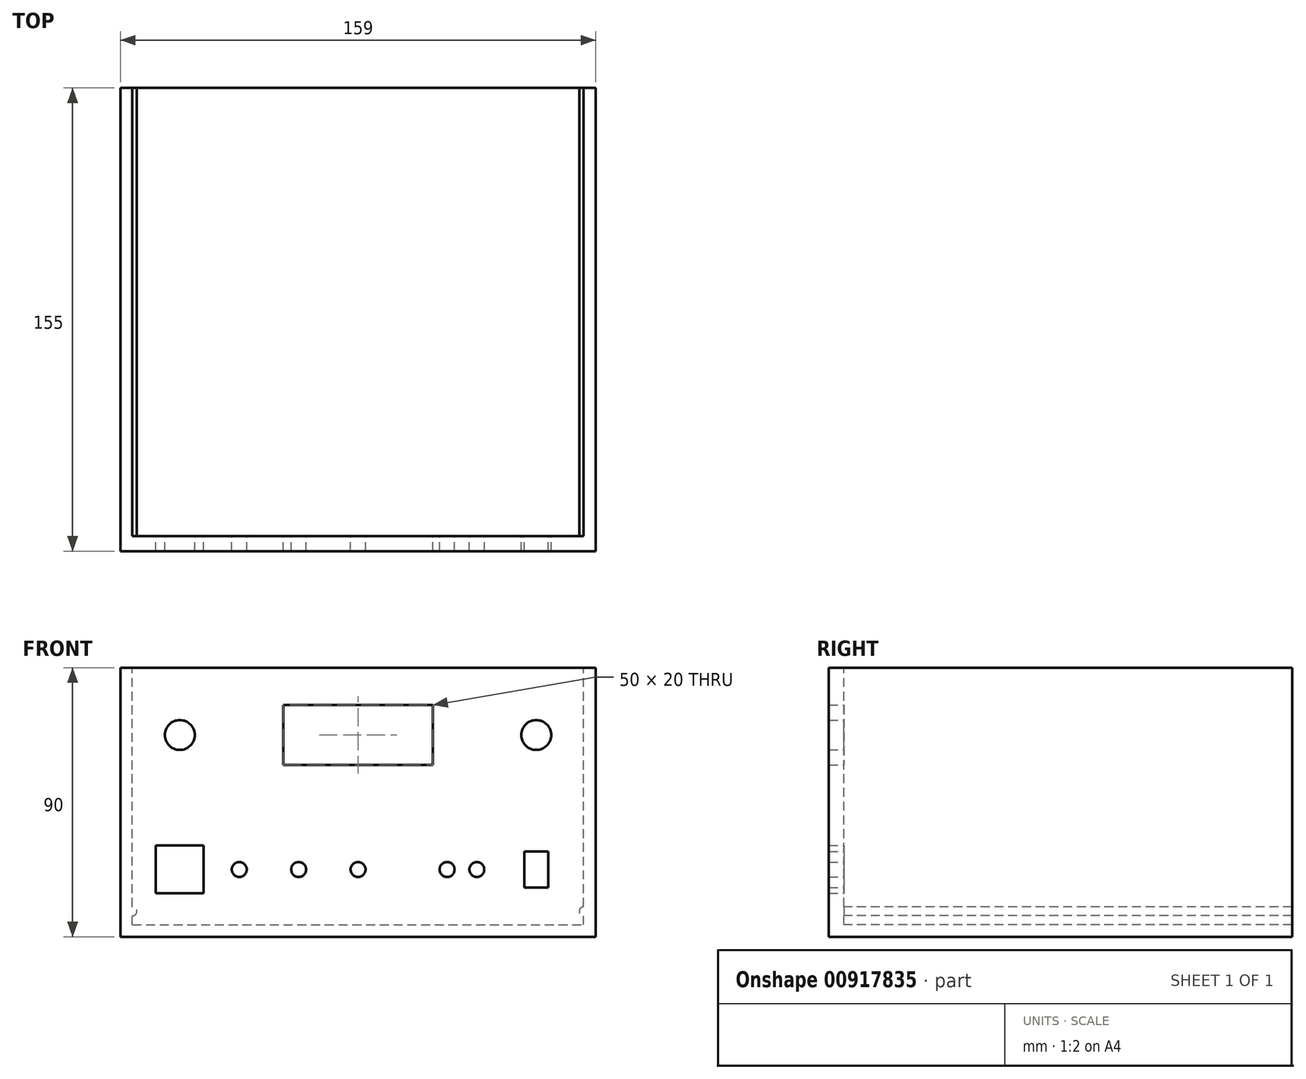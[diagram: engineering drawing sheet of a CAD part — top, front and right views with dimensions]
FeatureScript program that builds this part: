
annotation { "Feature Type Name" : "Feature", "Feature Type Description" : "" }
export const myFeature = defineFeature(function(context is Context, id is Id, definition is map)
    precondition{}
    {
        {
            var Q0;
            Q0=qCreatedBy(makeId("Front.planeOp"),FACE);
            var sketch = newSketch(context, id + "F0", { "sketchPlane" : qUnion([Q0])});
            skLineSegment(sketch, "E0.bottom", {"start": v(-79.5, 0) * mm, "end": v(79.5, 0) * mm});
            skLineSegment(sketch, "E0.top", {"start": v(-79.5, 90) * mm, "end": v(79.5, 90) * mm});
            skLineSegment(sketch, "E0.left", {"start": v(-79.5, 0) * mm, "end": v(-79.5, 90) * mm});
            skLineSegment(sketch, "E0.right", {"start": v(79.5, 0) * mm, "end": v(79.5, 90) * mm});
            skLineSegment(sketch, "E1", {"start": v(-79.5, 45) * mm, "end": v(0, 45) * mm, "construction": true});
            skLineSegment(sketch, "E2", {"start": v(0, 45) * mm, "end": v(-39.75, 45) * mm, "construction": true});
            skLineSegment(sketch, "E3", {"start": v(79.5, 45) * mm, "end": v(0, 45) * mm, "construction": true});
            skLineSegment(sketch, "E4", {"start": v(0, 45) * mm, "end": v(39.75, 45) * mm, "construction": true});
            skLineSegment(sketch, "E5", {"start": v(39.75, 45) * mm, "end": v(39.75, 90) * mm, "construction": true});
            skLineSegment(sketch, "E6", {"start": v(-39.75, 45) * mm, "end": v(-39.75, 90) * mm, "construction": true});
            skLineSegment(sketch, "E7", {"start": v(-39.75, 67.5) * mm, "end": v(39.75, 67.5) * mm, "construction": true});
            skLineSegment(sketch, "E8.MirrorCS", {"start": v(39.75, 45) * mm, "end": v(39.75, 0) * mm, "construction": true});
            skLineSegment(sketch, "E9.MirrorCS", {"start": v(-39.75, 45) * mm, "end": v(-39.75, 0) * mm, "construction": true});
            skLineSegment(sketch, "E10", {"start": v(-39.75, 67.5) * mm, "end": v(-79.5, 67.5) * mm, "construction": true});
            skLineSegment(sketch, "E11", {"start": v(-59.63, 67.5) * mm, "end": v(-59.63, 0) * mm, "construction": true});
            skPoint(sketch, "E11.endSnap0", {"position": v(-59.63, 67.5) * mm});
            skLineSegment(sketch, "E12", {"start": v(39.75, 67.5) * mm, "end": v(79.5, 67.5) * mm, "construction": true});
            skLineSegment(sketch, "E13", {"start": v(79.5, 67.5) * mm, "end": v(59.63, 67.5) * mm, "construction": true});
            skLineSegment(sketch, "E14", {"start": v(59.63, 67.5) * mm, "end": v(59.63, 0) * mm, "construction": true});
            skCircle(sketch, "E15", {"center": v(-59.63, 67.5) * mm, "radius": 5 * mm});
            skCircle(sketch, "E16", {"center": v(59.63, 67.5) * mm, "radius": 5 * mm});
            skLineSegment(sketch, "E17", {"start": v(0, 45) * mm, "end": v(0, 0) * mm, "construction": true});
            skLineSegment(sketch, "E18", {"start": v(0, 22.5) * mm, "end": v(-19.87, 22.5) * mm, "construction": true});
            skPoint(sketch, "E18.endSnap0", {"position": v(-19.88, 45) * mm});
            skLineSegment(sketch, "E19", {"start": v(-19.87, 22.5) * mm, "end": v(-39.75, 22.5) * mm, "construction": true});
            skLineSegment(sketch, "E20.MirrorCS", {"start": v(0, 22.5) * mm, "end": v(19.87, 22.5) * mm, "construction": true});
            skLineSegment(sketch, "E21.MirrorCS", {"start": v(19.87, 22.5) * mm, "end": v(39.75, 22.5) * mm, "construction": true});
            skCircle(sketch, "E22", {"center": v(39.75, 22.5) * mm, "radius": 2.5 * mm});
            skCircle(sketch, "E23", {"center": v(29.81, 22.5) * mm, "radius": 2.5 * mm});
            skCircle(sketch, "E24", {"center": v(-39.75, 22.5) * mm, "radius": 2.5 * mm});
            skCircle(sketch, "E25", {"center": v(-19.87, 22.5) * mm, "radius": 2.5 * mm});
            skLineSegment(sketch, "E26.bottom", {"start": v(63.63, 28.5) * mm, "end": v(55.63, 28.5) * mm});
            skLineSegment(sketch, "E26.top", {"start": v(63.63, 16.5) * mm, "end": v(55.63, 16.5) * mm});
            skLineSegment(sketch, "E26.left", {"start": v(63.63, 28.5) * mm, "end": v(63.63, 16.5) * mm});
            skLineSegment(sketch, "E26.right", {"start": v(55.63, 28.5) * mm, "end": v(55.63, 16.5) * mm});
            skPoint(sketch, "E26.middle", {"position": v(59.63, 22.5) * mm});
            skCircle(sketch, "E27", {"center": v(0, 22.5) * mm, "radius": 2.5 * mm});
            skLineSegment(sketch, "E28.bottom", {"start": v(25, 77.5) * mm, "end": v(-25, 77.5) * mm});
            skLineSegment(sketch, "E28.top", {"start": v(25, 57.5) * mm, "end": v(-25, 57.5) * mm});
            skLineSegment(sketch, "E28.left", {"start": v(25, 77.5) * mm, "end": v(25, 57.5) * mm});
            skLineSegment(sketch, "E28.right", {"start": v(-25, 77.5) * mm, "end": v(-25, 57.5) * mm});
            skPoint(sketch, "E28.middle", {"position": v(0, 67.5) * mm});
            skLineSegment(sketch, "E29.bottom", {"start": v(-51.62, 30.5) * mm, "end": v(-67.62, 30.5) * mm});
            skLineSegment(sketch, "E29.top", {"start": v(-51.62, 14.5) * mm, "end": v(-67.62, 14.5) * mm});
            skLineSegment(sketch, "E29.left", {"start": v(-51.62, 30.5) * mm, "end": v(-51.62, 14.5) * mm});
            skLineSegment(sketch, "E29.right", {"start": v(-67.62, 30.5) * mm, "end": v(-67.62, 14.5) * mm});
            skPoint(sketch, "E29.middle", {"position": v(-59.63, 22.5) * mm});
            skSolve(sketch);
        }
        {
            var Q0;
            Q0=makeQuery(id+"F0.imprint","IMPRINT",FACE,{"disambiguationData":[TD([[makeQuery(id+"F0.imprint","IMPRINT",EDGE,{"derivedFrom":sQuery(id+"F0.wireOp",EDGE,"E0.bottom")}),1.0]])]});
            extrude(context, id + "F1", {"entities" : qUnion([Q0]), "depth" : 5 * mm, "offsetDistance" : 25 * mm});
        }
        {
            var Q0;
            Q0=makeQuery(id+"F1.opExtrude","CAP_FACE",FACE,{"disambiguationData":[OSD([sQuery(id+"F0.wireOp",EDGE,"E0.bottom"),sQuery(id+"F0.wireOp",EDGE,"E0.top"),sQuery(id+"F0.wireOp",EDGE,"E0.left"),sQuery(id+"F0.wireOp",EDGE,"E0.right"),sQuery(id+"F0.wireOp",EDGE,"E15"),sQuery(id+"F0.wireOp",EDGE,"E16"),sQuery(id+"F0.wireOp",EDGE,"E22"),sQuery(id+"F0.wireOp",EDGE,"E23"),sQuery(id+"F0.wireOp",EDGE,"E24"),sQuery(id+"F0.wireOp",EDGE,"E25"),sQuery(id+"F0.wireOp",EDGE,"E26.bottom"),sQuery(id+"F0.wireOp",EDGE,"E26.top"),sQuery(id+"F0.wireOp",EDGE,"E26.left"),sQuery(id+"F0.wireOp",EDGE,"E26.right"),sQuery(id+"F0.wireOp",EDGE,"E27"),sQuery(id+"F0.wireOp",EDGE,"E28.bottom"),sQuery(id+"F0.wireOp",EDGE,"E28.top"),sQuery(id+"F0.wireOp",EDGE,"E28.left"),sQuery(id+"F0.wireOp",EDGE,"E28.right"),sQuery(id+"F0.wireOp",EDGE,"E29.bottom"),sQuery(id+"F0.wireOp",EDGE,"E29.top"),sQuery(id+"F0.wireOp",EDGE,"E29.left"),sQuery(id+"F0.wireOp",EDGE,"E29.right")])],"isStart":true});
            var sketch = newSketch(context, id + "F2", { "sketchPlane" : qUnion([Q0])});
            skLineSegment(sketch, "E30.0", {"start": v(-75.5, 4) * mm, "end": v(-75.5, 7) * mm});
            skLineSegment(sketch, "E30.1", {"start": v(75.5, 4) * mm, "end": v(-75.5, 4) * mm});
            skLineSegment(sketch, "E30.2", {"start": v(75.5, 4) * mm, "end": v(75.5, 7) * mm});
            skArc(sketch, "E31", {"start": v(-75.5, 7) * mm, "mid": v(-74, 8.5) * mm, "end": v(-75.5, 10) * mm});
            skLineSegment(sketch, "E32", {"start": v(0, 4) * mm, "end": v(0, 57.5) * mm, "construction": true});
            skArc(sketch, "E33.MirrorCS", {"start": v(75.5, 7) * mm, "mid": v(74, 8.5) * mm, "end": v(75.5, 10) * mm});
            skLineSegment(sketch, "E34.trimOffspring", {"start": v(-75.5, 10) * mm, "end": v(-75.5, 90) * mm});
            skLineSegment(sketch, "E35.trimOffspring", {"start": v(75.5, 10) * mm, "end": v(75.5, 90) * mm});
            skSolve(sketch);
        }
        {
            var Q0;
            {var subQ3=sQuery(id+"F2.wireOp",EDGE,"E30.0");Q0=makeQuery(id+"F2.imprint","IMPRINT",FACE,{"disambiguationData":[TD([[makeQuery(id+"F2.imprint","IMPRINT",EDGE,{"derivedFrom":subQ3}),1.0]])]});}
            extrude(context, id + "F3", {"entities" : qUnion([Q0]), "operationType" : NewBodyOperationType.ADD, "depth" : 150 * mm, "offsetDistance" : 25 * mm});
        }
    });
